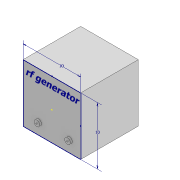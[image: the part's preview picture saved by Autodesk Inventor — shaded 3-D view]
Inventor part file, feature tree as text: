
AUTODESK INVENTOR PART (.ipt)
format: ipt  version: 2021 (Build 250183000, 183)  size: 100,352 bytes
history: native  units: mm
features: sketch x4, extrude x3, other x2
ambient origin geometry x8: Origin, YZ Plane, XZ Plane, XY Plane, X Axis, Y Axis, Z Axis, Center Point
bodies: Body1 (feature_tree)
feature tree (9):
  other  "Твердое тело1"
  sketch  "Эскиз1"
  extrude  "Выдавливание1"  Depth=10.0mm
  sketch  "Эскиз2"
  other  "РабПлоскость1"
  extrude  "Выдавливание2"  Depth=10.0mm
  extrude  "Выдавливание3"  Depth=10.0mm TaperAngle=0.0deg
  sketch  "Эскиз3"
  sketch  "Эскиз4"
